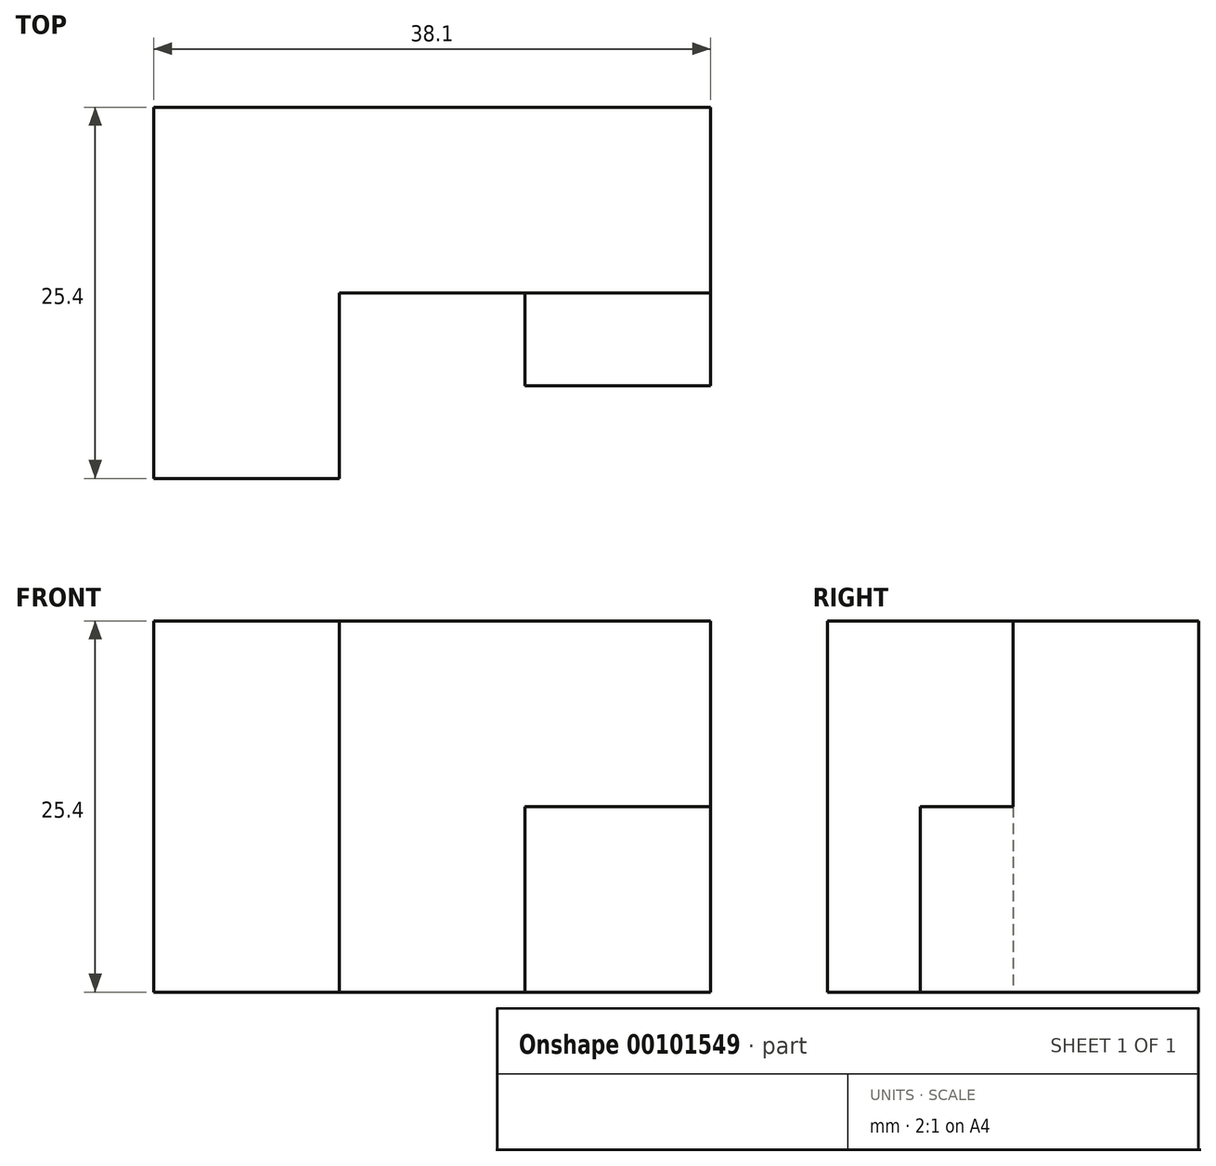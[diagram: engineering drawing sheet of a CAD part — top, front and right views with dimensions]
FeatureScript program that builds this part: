
annotation { "Feature Type Name" : "Feature", "Feature Type Description" : "" }
export const myFeature = defineFeature(function(context is Context, id is Id, definition is map)
    precondition{}
    {
        {
            var Q0;
            Q0=qCreatedBy(makeId("Top.planeOp"),FACE);
            var sketch = newSketch(context, id + "F0", { "sketchPlane" : qUnion([Q0])});
            skLineSegment(sketch, "E0", {"start": v(0, 0) * mm, "end": v(0, 25.4) * mm});
            skLineSegment(sketch, "E1", {"start": v(0, 25.4) * mm, "end": v(38.1, 25.4) * mm});
            skLineSegment(sketch, "E2", {"start": v(38.1, 25.4) * mm, "end": v(38.1, 12.7) * mm});
            skLineSegment(sketch, "E3", {"start": v(12.7, 12.7) * mm, "end": v(12.7, 0) * mm});
            skLineSegment(sketch, "E4", {"start": v(12.7, 0) * mm, "end": v(0, 0) * mm});
            skLineSegment(sketch, "E5", {"start": v(25.4, 12.7) * mm, "end": v(25.4, 6.35) * mm});
            skLineSegment(sketch, "E6", {"start": v(25.4, 6.35) * mm, "end": v(38.1, 6.35) * mm});
            skLineSegment(sketch, "E7", {"start": v(38.1, 6.35) * mm, "end": v(38.1, 12.7) * mm});
            skLineSegment(sketch, "E8", {"start": v(25.4, 12.7) * mm, "end": v(38.1, 12.7) * mm});
            skLineSegment(sketch, "E9", {"start": v(25.4, 12.7) * mm, "end": v(12.7, 12.7) * mm});
            skSolve(sketch);
        }
        {
            var Q0;
            Q0=makeQuery(id+"F0.imprint","IMPRINT",FACE,{"disambiguationData":[TD([[makeQuery(id+"F0.imprint","IMPRINT",EDGE,{"derivedFrom":sQuery(id+"F0.wireOp",EDGE,"E0")}),-1.0]])]});
            extrude(context, id + "F1", {"entities" : qUnion([Q0]), "depth" : 25.4 * mm});
        }
        {
            var Q0;
            Q0=makeQuery(id+"F0.imprint","IMPRINT",FACE,{"disambiguationData":[TD([[makeQuery(id+"F0.imprint","IMPRINT",EDGE,{"derivedFrom":sQuery(id+"F0.wireOp",EDGE,"E5")}),1.0]])]});
            extrude(context, id + "F2", {"entities" : qUnion([Q0]), "operationType" : NewBodyOperationType.ADD, "depth" : 12.7 * mm});
        }
    });
